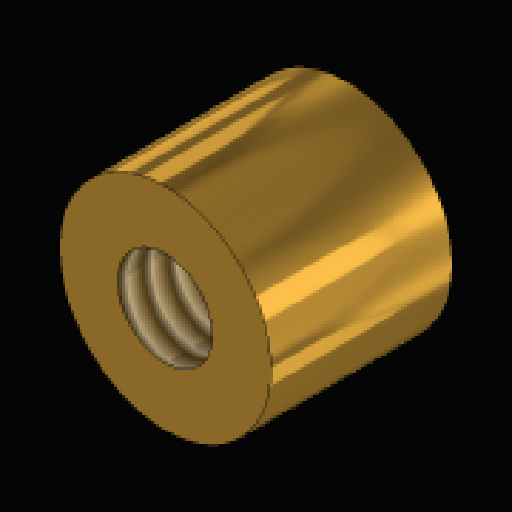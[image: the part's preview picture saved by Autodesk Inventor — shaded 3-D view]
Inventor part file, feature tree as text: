
AUTODESK INVENTOR PART (.ipt)
format: ipt  version: 2023.2 (Build 272271030, 271C)  size: 112,128 bytes
history: native  units: mm
features: sketch x2, extrude x1, hole x1
ambient origin geometry x8: Origin, YZ Plane, XZ Plane, XY Plane, X Axis, Y Axis, Z Axis, Center Point
bodies: Solid1 (feature_tree)
feature tree (4):
  extrude  "Extrusion1"  Depth=3.0mm TaperAngle=0.0deg
  hole  "Hole1"  [1 undecoded]
  sketch  "Sketch1"  dims[d0=3.5mm d1=3.0mm d2=0.0mm]
  sketch  "Sketch2"  dims[d3=1.567mm d4=4.0mm d5=4.0mm d6=2.0mm d7=90.0deg d8=6.3mm d9=20.594885mm]
note: 1 required parameter value undecoded (feature->parameter linkage not recoverable at this tier; creation-order binding heuristic only, values carry confidence <= 0.55)
